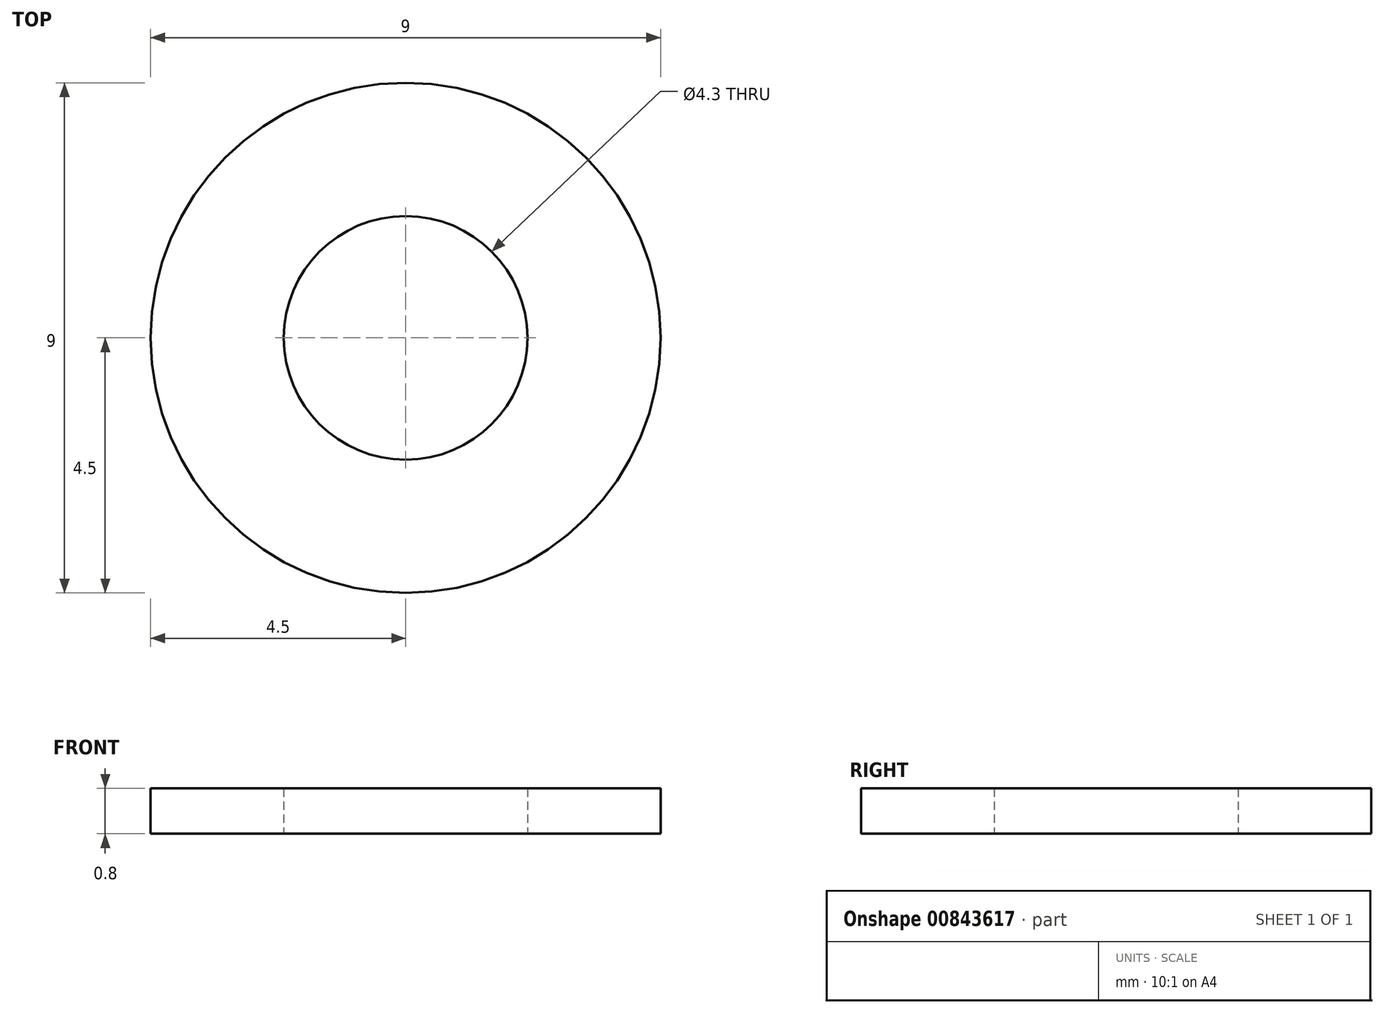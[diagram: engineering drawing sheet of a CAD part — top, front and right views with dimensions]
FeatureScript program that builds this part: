
annotation { "Feature Type Name" : "Feature", "Feature Type Description" : "" }
export const myFeature = defineFeature(function(context is Context, id is Id, definition is map)
    precondition{}
    {
        {
            var Q0;
            Q0=qCreatedBy(makeId("Top.planeOp"),FACE);
            var sketch = newSketch(context, id + "F0", { "sketchPlane" : qUnion([Q0])});
            skCircle(sketch, "E0", {"center": v(0, 0) * mm, "radius": 2.15 * mm});
            skCircle(sketch, "E1", {"center": v(0, 0) * mm, "radius": 4.5 * mm});
            skSolve(sketch);
        }
        {
            var Q0;
            Q0=makeQuery(id+"F0.imprint","IMPRINT",FACE,{"disambiguationData":[TD([[makeQuery(id+"F0.imprint","IMPRINT",EDGE,{"derivedFrom":sQuery(id+"F0.wireOp",EDGE,"E0")}),-1.0]])]});
            extrude(context, id + "F1", {"entities" : qUnion([Q0]), "depth" : .8 * mm, "offsetDistance" : 25 * mm});
        }
    });
